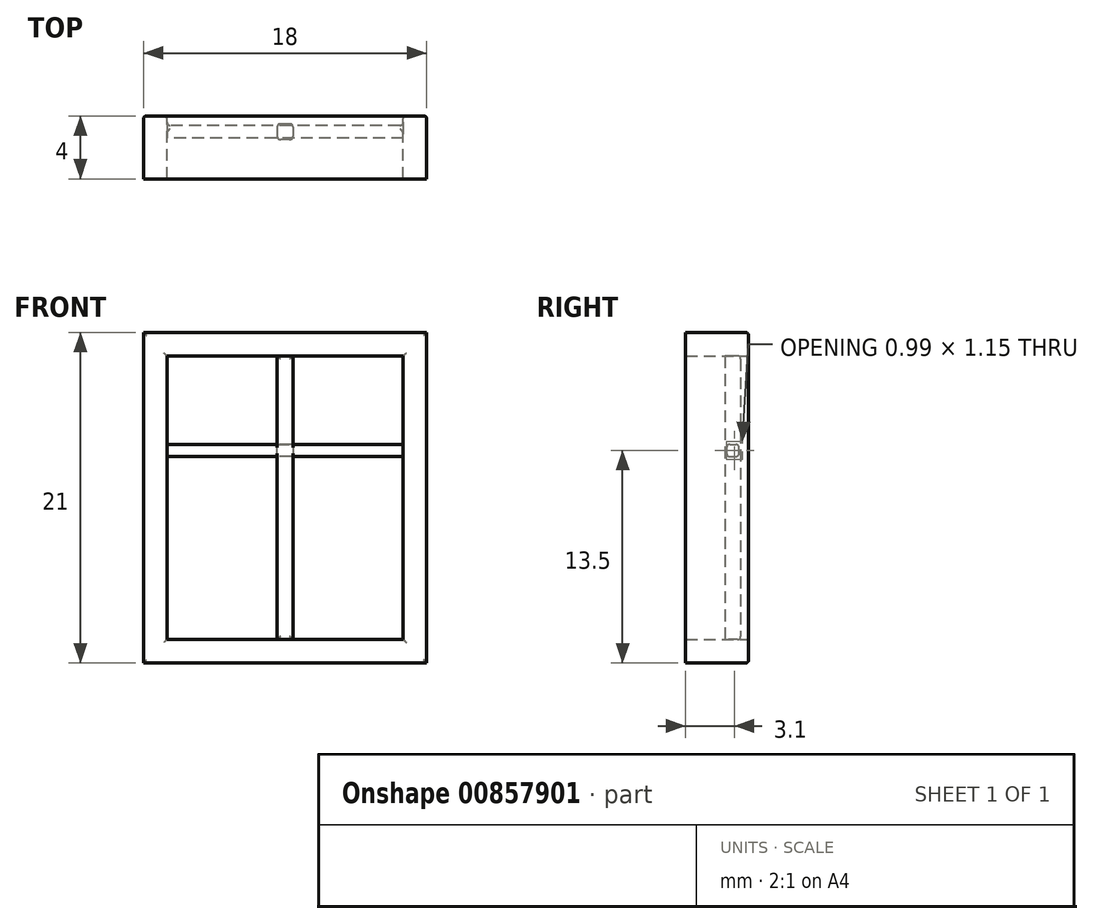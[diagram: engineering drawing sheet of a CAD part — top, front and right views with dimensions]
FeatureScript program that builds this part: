
annotation { "Feature Type Name" : "Feature", "Feature Type Description" : "" }
export const myFeature = defineFeature(function(context is Context, id is Id, definition is map)
    precondition{}
    {
        {
            var Q0;
            Q0=qCreatedBy(makeId("Front.planeOp"),FACE);
            var sketch = newSketch(context, id + "F0", { "sketchPlane" : qUnion([Q0])});
            skLineSegment(sketch, "E0.bottom", {"start": v(7.5, 0) * mm, "end": v(-7.5, 0) * mm});
            skLineSegment(sketch, "E0.top", {"start": v(7.5, 18) * mm, "end": v(-7.5, 18) * mm});
            skLineSegment(sketch, "E0.left", {"start": v(7.5, 0) * mm, "end": v(7.5, 18) * mm});
            skLineSegment(sketch, "E0.right", {"start": v(-7.5, 0) * mm, "end": v(-7.5, 18) * mm});
            skPoint(sketch, "E0.middle", {"position": v(0, 9) * mm});
            skLineSegment(sketch, "E1.0", {"start": v(-9, -1.5) * mm, "end": v(-9, 19.5) * mm});
            skLineSegment(sketch, "E1.1", {"start": v(9, -1.5) * mm, "end": v(-9, -1.5) * mm});
            skLineSegment(sketch, "E1.2", {"start": v(9, -1.5) * mm, "end": v(9, 19.5) * mm});
            skLineSegment(sketch, "E1.3", {"start": v(9, 19.5) * mm, "end": v(-9, 19.5) * mm});
            skPoint(sketch, "E2", {"position": v(0, 19.5) * mm});
            skLineSegment(sketch, "E3", {"start": v(0, 0) * mm, "end": v(0, 18) * mm});
            skLineSegment(sketch, "E4", {"start": v(-7.5, 12) * mm, "end": v(7.5, 12) * mm});
            skLineSegment(sketch, "E5", {"start": v(0, 23.5) * mm, "end": v(0, -2.7) * mm, "construction": true});
            skPoint(sketch, "E5.startSnap0", {"position": v(0, -1.5) * mm});
            skSolve(sketch);
        }
        {
            var Q0;
            Q0=makeQuery(id+"F0.imprint","IMPRINT",FACE,{"disambiguationData":[TD([[makeQuery(id+"F0.imprint","IMPRINT",EDGE,{"derivedFrom":sQuery(id+"F0.wireOp",EDGE,"E1.0")}),-1.0]])]});
            extrude(context, id + "F1", {"entities" : qUnion([Q0]), "depth" : 3 * mm, "offsetDistance" : 25 * mm});
        }
        {
            var Q0;
            Q0=makeQuery(id+"F0.imprint","IMPRINT",FACE,{"disambiguationData":[TD([[makeQuery(id+"F0.imprint","IMPRINT",EDGE,{"derivedFrom":sQuery(id+"F0.wireOp",EDGE,"E1.0")}),-1.0]])]});
            extrude(context, id + "F2", {"entities" : qUnion([Q0]), "operationType" : NewBodyOperationType.ADD, "oppositeDirection" : true, "depth" : 1 * mm, "offsetDistance" : 25 * mm});
        }
        {
            var Q0;
            {var subQ0=sQuery(id+"F0.wireOp",EDGE,"E0.right");Q0=makeQuery(id+"F2.boolean.opBoolean","MERGE",FACE,{"derivedFrom":[makeQuery(id+"F1.opExtrude","SWEPT_FACE",FACE,{"disambiguationData":[OSD([subQ0])]}),makeQuery(id+"F2.opExtrude","SWEPT_FACE",FACE,{"disambiguationData":[OSD([subQ0])]})]});}
            var sketch = newSketch(context, id + "F3", { "sketchPlane" : qUnion([Q0])});
            skLineSegment(sketch, "E6.bottom", {"start": v(0.4, 11.62) * mm, "end": v(-0.4, 11.62) * mm});
            skLineSegment(sketch, "E6.top", {"start": v(0.4, 12.38) * mm, "end": v(-0.4, 12.38) * mm});
            skLineSegment(sketch, "E6.left", {"start": v(0.4, 11.62) * mm, "end": v(0.4, 12.38) * mm});
            skLineSegment(sketch, "E6.right", {"start": v(-0.4, 11.62) * mm, "end": v(-0.4, 12.38) * mm});
            skPoint(sketch, "E6.middle", {"position": v(0, 12) * mm});
            skSolve(sketch);
        }
        {
            var Q0;
            Q0 = qSketchRegion(id + "F3", true);
            extrude(context, id + "F4", {"entities" : qUnion([Q0]), "operationType" : NewBodyOperationType.ADD, "endBound" : BoundingType.UP_TO_NEXT, "depth" : 25 * mm, "offsetDistance" : 25 * mm});
        }
        {
            var Q0;
            {var subQ0=sQuery(id+"F0.wireOp",EDGE,"E0.top");Q0=makeQuery(id+"F2.boolean.opBoolean","MERGE",FACE,{"derivedFrom":[makeQuery(id+"F1.opExtrude","SWEPT_FACE",FACE,{"disambiguationData":[OSD([subQ0])]}),makeQuery(id+"F2.opExtrude","SWEPT_FACE",FACE,{"disambiguationData":[OSD([subQ0])]})]});}
            var sketch = newSketch(context, id + "F5", { "sketchPlane" : qUnion([Q0])});
            skLineSegment(sketch, "E7.bottom", {"start": v(0.5, -0.5) * mm, "end": v(-0.5, -0.5) * mm});
            skLineSegment(sketch, "E7.top", {"start": v(0.5, 0.5) * mm, "end": v(-0.5, 0.5) * mm});
            skLineSegment(sketch, "E7.left", {"start": v(0.5, -0.5) * mm, "end": v(0.5, 0.5) * mm});
            skLineSegment(sketch, "E7.right", {"start": v(-0.5, -0.5) * mm, "end": v(-0.5, 0.5) * mm});
            skPoint(sketch, "E7.middle", {"position": v(0, 0) * mm});
            skSolve(sketch);
        }
        {
            var Q0;
            Q0 = qSketchRegion(id + "F5", true);
            var Q1;
            {var subQ0=sQuery(id+"F0.wireOp",EDGE,"E0.bottom");Q1=makeQuery(id+"F2.boolean.opBoolean","MERGE",FACE,{"derivedFrom":[makeQuery(id+"F1.opExtrude","SWEPT_FACE",FACE,{"disambiguationData":[OSD([subQ0])]}),makeQuery(id+"F2.opExtrude","SWEPT_FACE",FACE,{"disambiguationData":[OSD([subQ0])]})]});}
            extrude(context, id + "F6", {"entities" : qUnion([Q0]), "endBound" : BoundingType.UP_TO_SURFACE, "depth" : 25 * mm, "endBoundEntityFace" : qUnion([Q1]), "offsetDistance" : 25 * mm});
        }
        {
            var Q0;
            Q0=makeQuery(id+"F6.opExtrude","SWEPT_FACE",FACE,{"disambiguationData":[OSD([sQuery(id+"F5.wireOp",EDGE,"E7.bottom")])]});
            var Q1;
            Q1=makeQuery(id+"F4.opExtrude","SWEPT_EDGE",EDGE,{"disambiguationData":[OSD([sQuery(id+"F3.wireOp",EDGE,"E6.top"),sQuery(id+"F3.wireOp",EDGE,"E6.right")])]});
            var Q2;
            Q2=makeQuery(id+"F4.opExtrude","SWEPT_EDGE",EDGE,{"disambiguationData":[OSD([sQuery(id+"F3.wireOp",EDGE,"E6.bottom"),sQuery(id+"F3.wireOp",EDGE,"E6.right")])]});
            var Q3;
            Q3=makeQuery(id+"F6.opExtrude","SWEPT_EDGE",EDGE,{"disambiguationData":[OSD([sQuery(id+"F5.wireOp",EDGE,"E7.top"),sQuery(id+"F5.wireOp",EDGE,"E7.left")])]});
            var Q4;
            Q4=makeQuery(id+"F6.opExtrude","SWEPT_EDGE",EDGE,{"disambiguationData":[OSD([sQuery(id+"F5.wireOp",EDGE,"E7.top"),sQuery(id+"F5.wireOp",EDGE,"E7.right")])]});
            fillet(context, id + "F7", {"entities" : qUnion([Q0, Q1, Q2, Q3, Q4]), "radius" : .2 * mm, "tangentPropagation" : true, "rho" : 0.5, "crossSection" : FilletCrossSection.CONIC, "allowEdgeOverflow" : false});
        }
        {
            var Q0;
            Q0=makeQuery(id+"F4.opExtrude","SWEPT_FACE",FACE,{"disambiguationData":[OSD([sQuery(id+"F3.wireOp",EDGE,"E6.left")])]});
            fillet(context, id + "F8", {"entities" : qUnion([Q0]), "radius" : .2 * mm, "allowEdgeOverflow" : false});
        }
        {
            var Q0;
            Q0=makeQuery(id+"F2.opExtrude","CAP_FACE",FACE,{"disambiguationData":[OSD([sQuery(id+"F0.wireOp",EDGE,"E0.bottom"),sQuery(id+"F0.wireOp",EDGE,"E0.top"),sQuery(id+"F0.wireOp",EDGE,"E0.left"),sQuery(id+"F0.wireOp",EDGE,"E0.right"),sQuery(id+"F0.wireOp",EDGE,"E1.0"),sQuery(id+"F0.wireOp",EDGE,"E1.1"),sQuery(id+"F0.wireOp",EDGE,"E1.2"),sQuery(id+"F0.wireOp",EDGE,"E1.3")])],"isStart":false});
            fillet(context, id + "F9", {"entities" : qUnion([Q0]), "radius" : .2 * mm, "tangentPropagation" : true, "allowEdgeOverflow" : false});
        }
    });
